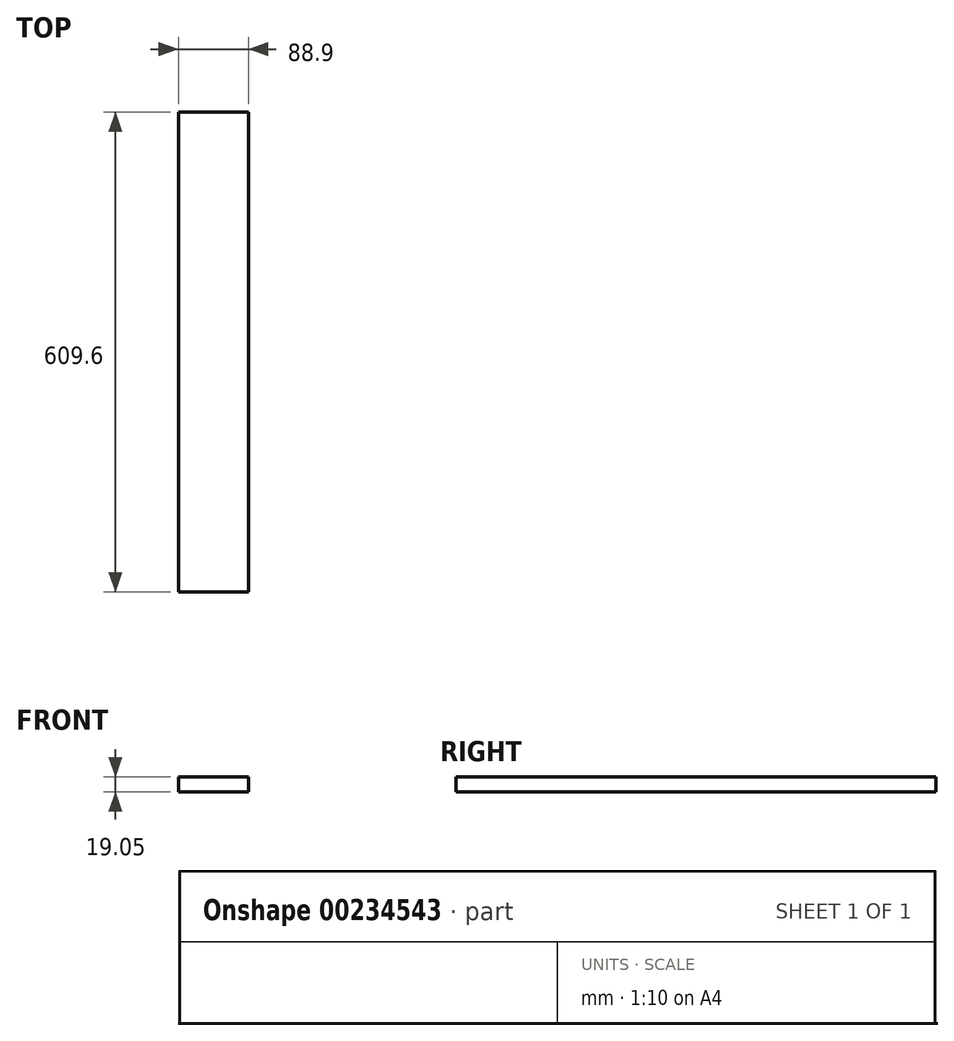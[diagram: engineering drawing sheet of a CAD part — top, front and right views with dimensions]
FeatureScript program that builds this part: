
annotation { "Feature Type Name" : "Feature", "Feature Type Description" : "" }
export const myFeature = defineFeature(function(context is Context, id is Id, definition is map)
    precondition{}
    {
        {
            var Q0;
            Q0=qCreatedBy(makeId("Top.planeOp"),FACE);
            var sketch = newSketch(context, id + "F0", { "sketchPlane" : qUnion([Q0])});
            skLineSegment(sketch, "E0.bottom", {"start": v(0, 0) * mm, "end": v(88.9, 0) * mm});
            skLineSegment(sketch, "E0.top", {"start": v(0, 609.6) * mm, "end": v(88.9, 609.6) * mm});
            skLineSegment(sketch, "E0.left", {"start": v(0, 0) * mm, "end": v(0, 609.6) * mm});
            skLineSegment(sketch, "E0.right", {"start": v(88.9, 0) * mm, "end": v(88.9, 609.6) * mm});
            skSolve(sketch);
        }
        {
            var Q0;
            Q0 = qSketchRegion(id + "F0", true);
            extrude(context, id + "F1", {"entities" : qUnion([Q0]), "depth" : 19.05 * mm});
        }
    });
